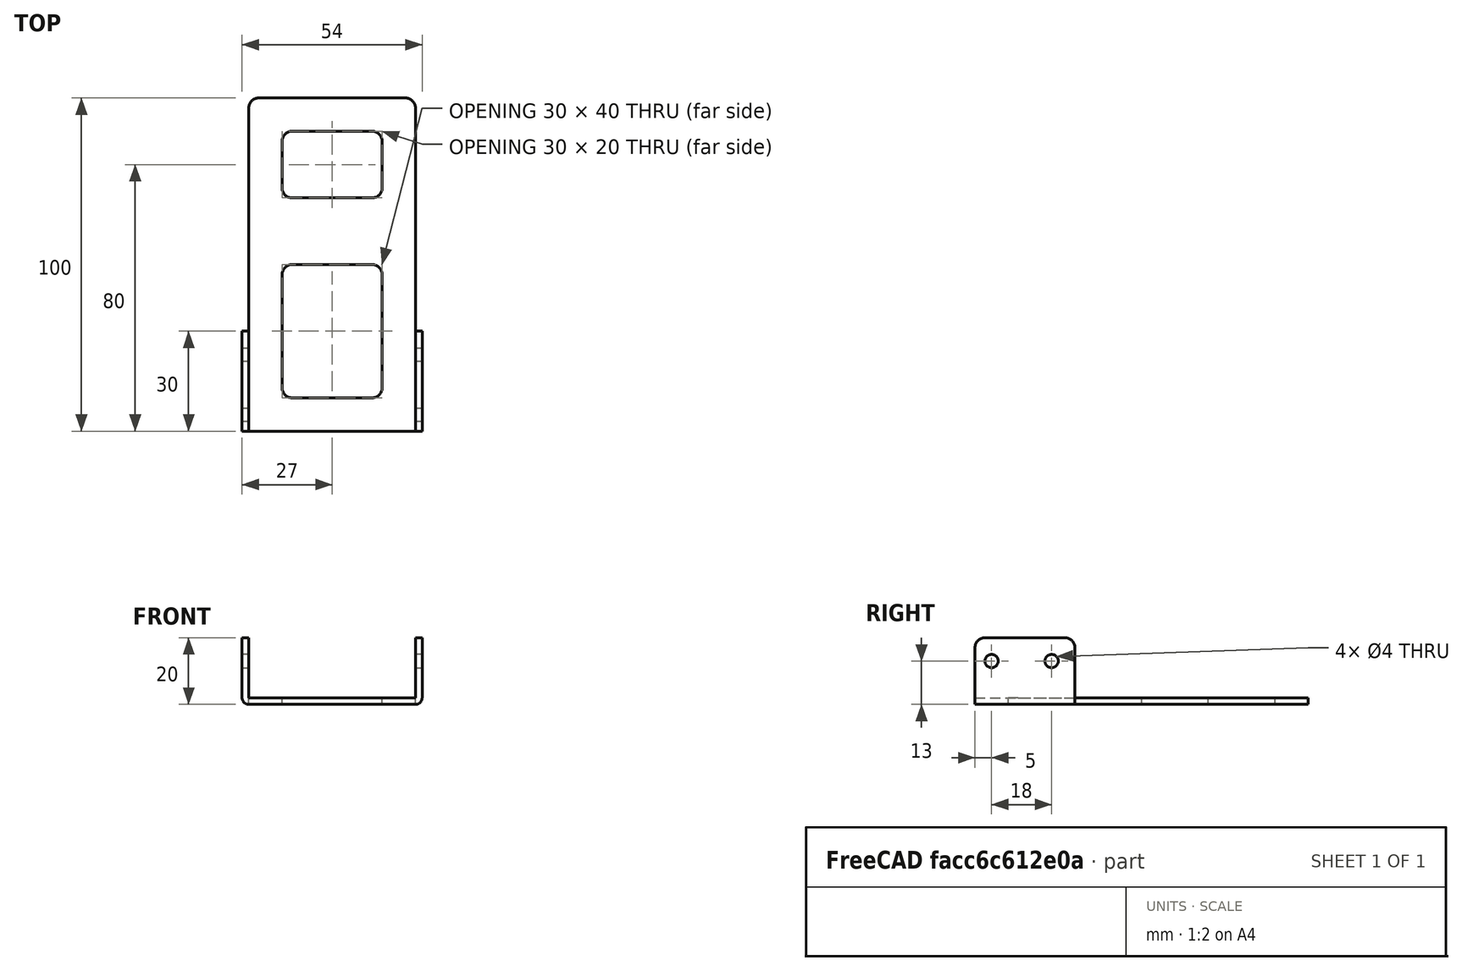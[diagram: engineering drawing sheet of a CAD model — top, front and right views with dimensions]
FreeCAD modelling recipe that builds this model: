
FCSTD DOCUMENT  (FreeCAD 1.0R39319 (Git))
Label: ojt1_t12r03_universal_support
License: All rights reserved
LicenseURL: https://en.wikipedia.org/wiki/All_rights_reserved
objects: Part::Fillet×8, Part::Cut×6, Part::Box×5, Part::Cylinder×4, Part::MultiFuse×1
note: 24 computed .brp shape members not serialized (recipe doc carries the construction recipe); baked Part::Feature solids carry a one-line shape summary decoded from their .brp

FEATURE [Part::Box] Box  label="Cub"
  AttacherType = Attacher::AttachEngine3D
  Height = 2
  Length = 50
  Width = 100
FEATURE [Part::Box] Box001  label="Cub001"
  AttacherType = Attacher::AttachEngine3D
  Height = 10
  Length = 30
  Placement = pos=(10,70,0) rot=(0,0,1;0rad)
  Width = 20
FEATURE [Part::Fillet] Fillet
  Base = -> Box001
  EdgeLinks = -> Box001 [Edge1,Edge3,Edge5,Edge7]
  Edges = 4 edges r=3: [Edge1,Edge3,Edge5,Edge7]
  Placement = pos=(0,0,-5) rot=(0,0,1;0rad)
FEATURE [Part::Cut] Cut
  Base = -> Box
  Tool = -> Fillet
FEATURE [Part::Box] Box002  label="Cub002"
  AttacherType = Attacher::AttachEngine3D
  Height = 10
  Length = 30
  Placement = pos=(10,10,-2) rot=(0,0,1;0rad)
  Width = 40
FEATURE [Part::Fillet] Fillet001
  Base = -> Box002
  EdgeLinks = -> Box002 [Edge1,Edge3,Edge5,Edge7]
  Edges = 4 edges r=3: [Edge1,Edge3,Edge5,Edge7]
FEATURE [Part::Cut] Cut001
  Base = -> Cut
  Tool = -> Fillet001
FEATURE [Part::Fillet] Fillet002
  Base = -> Cut001
  EdgeLinks = -> Cut001 [Edge27]
  Edges = 1 edges r=3: [Edge27]
FEATURE [Part::Fillet] Fillet003  label="base final"
  Base = -> Fillet002
  EdgeLinks = -> Fillet002 [Edge24]
  Edges = 1 edges r=3: [Edge24]
FEATURE [Part::Box] Box003  label="Cub003"
  AttacherType = Attacher::AttachEngine3D
  Height = 20
  Length = 2
  Placement = pos=(-14,0,0) rot=(0,0,1;0rad)
  Width = 30
FEATURE [Part::Fillet] Fillet004
  Base = -> Box003
  EdgeLinks = -> Box003 [Edge10,Edge12]
  Edges = 2 edges r=3: [Edge10,Edge12]
FEATURE [Part::Cylinder] Cylinder  label="Cilindre"
  Angle = 360
  AttacherType = Attacher::AttachEngine3D
  FirstAngle = 0
  Height = 10
  Placement = pos=(-10,5,13) rot=(0,-1,0;1.5708rad)
  Radius = 2
  SecondAngle = 0
FEATURE [Part::Cylinder] Cylinder001  label="Cilindre001"
  Angle = 360
  AttacherType = Attacher::AttachEngine3D
  FirstAngle = 0
  Height = 10
  Placement = pos=(-10,23,13) rot=(0,-1,0;1.5708rad)
  Radius = 2
  SecondAngle = 0
FEATURE [Part::Cut] Cut002
  Base = -> Fillet004
  Tool = -> Cylinder
FEATURE [Part::Cut] Cut003
  Base = -> Cut002
  Placement = pos=(12,0,0) rot=(0,0,1;0rad)
  Tool = -> Cylinder001
FEATURE [Part::Box] Box004  label="Cub004"
  AttacherType = Attacher::AttachEngine3D
  Height = 20
  Length = 2
  Placement = pos=(-14,0,0) rot=(0,0,1;0rad)
  Width = 30
FEATURE [Part::Cylinder] Cylinder002  label="Cilindre002"
  Angle = 360
  AttacherType = Attacher::AttachEngine3D
  FirstAngle = 0
  Height = 10
  Placement = pos=(-10,5,13) rot=(0,-1,0;1.5708rad)
  Radius = 2
  SecondAngle = 0
FEATURE [Part::Cylinder] Cylinder003  label="Cilindre003"
  Angle = 360
  AttacherType = Attacher::AttachEngine3D
  FirstAngle = 0
  Height = 10
  Placement = pos=(-10,23,13) rot=(0,-1,0;1.5708rad)
  Radius = 2
  SecondAngle = 0
FEATURE [Part::Fillet] Fillet005
  Base = -> Box004
  EdgeLinks = -> Box004 [Edge10,Edge12]
  Edges = 2 edges r=3: [Edge10,Edge12]
FEATURE [Part::Cut] Cut004
  Base = -> Fillet005
  Tool = -> Cylinder002
FEATURE [Part::Cut] Cut005
  Base = -> Cut004
  Placement = pos=(64,0,0) rot=(0,0,1;0rad)
  Tool = -> Cylinder003
FEATURE [Part::MultiFuse] Fusion
  Refine = true
  Shapes = -> [Fillet003,Cut003,Cut005]
FEATURE [Part::Fillet] Fillet006
  Base = -> Fusion
  EdgeLinks = -> Fusion [Edge109]
  Edges = 1 edges r=2: [Edge109]
FEATURE [Part::Fillet] Fillet007
  Base = -> Fillet006
  EdgeLinks = -> Fillet006 [Edge35]
  Edges = 1 edges r=2: [Edge35]
